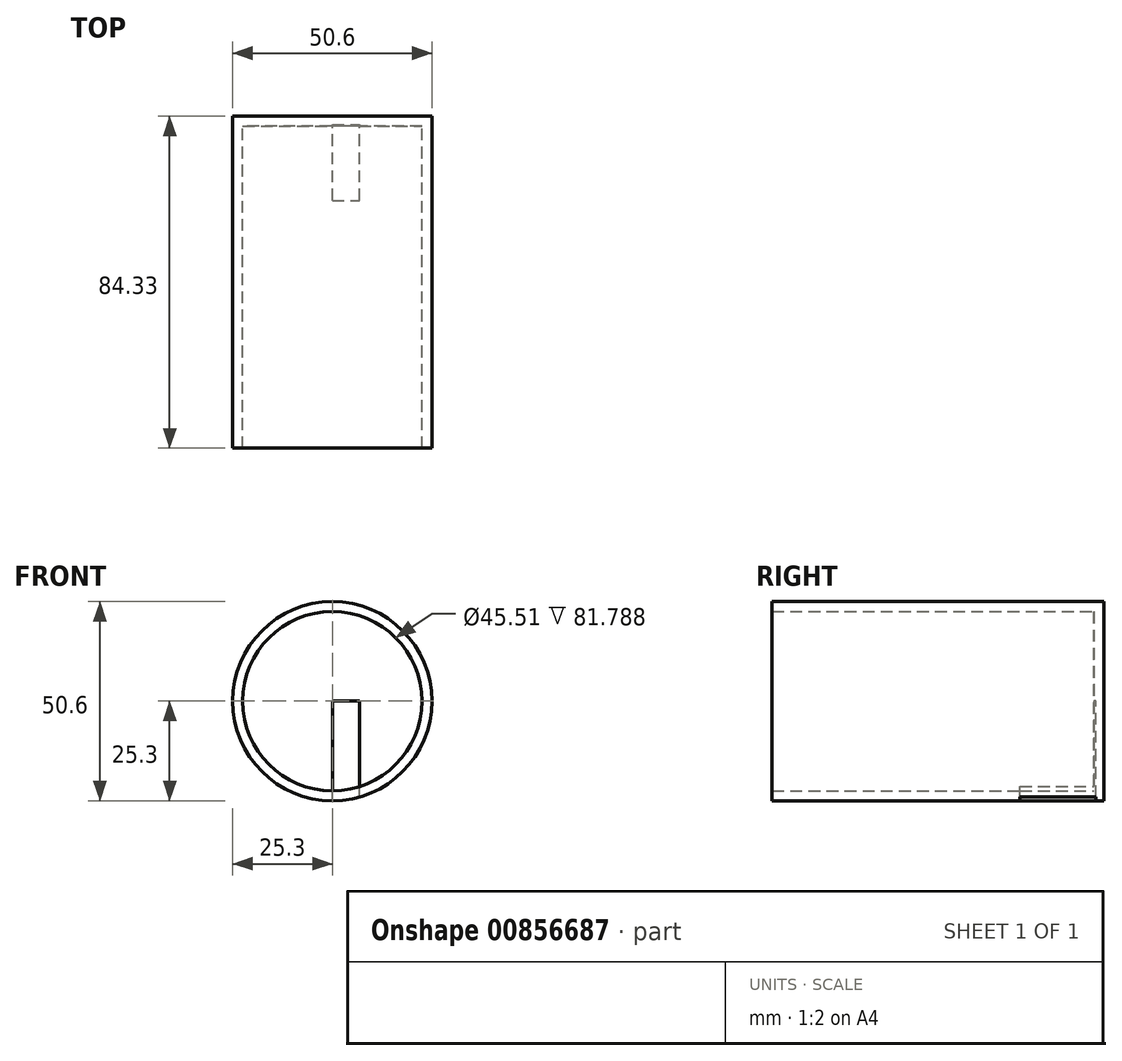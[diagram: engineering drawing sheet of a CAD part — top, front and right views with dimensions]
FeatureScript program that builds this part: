
annotation { "Feature Type Name" : "Feature", "Feature Type Description" : "" }
export const myFeature = defineFeature(function(context is Context, id is Id, definition is map)
    precondition{}
    {
        {
            var Q0;
            Q0=qCreatedBy(makeId("Front.planeOp"),FACE);
            var sketch = newSketch(context, id + "F0", { "sketchPlane" : qUnion([Q0])});
            skCircle(sketch, "E0", {"center": v(0, 0) * mm, "radius": 25.3 * mm});
            skSolve(sketch);
        }
        {
            var Q0;
            Q0 = qSketchRegion(id + "F0", true);
            extrude(context, id + "F1", {"entities" : qUnion([Q0]), "depth" : 84.33 * mm, "offsetDistance" : 25.4 * mm});
        }
        {
            var Q0;
            Q0=makeQuery(id+"F1.opExtrude","CAP_FACE",FACE,{"disambiguationData":[OSD([sQuery(id+"F0.wireOp",EDGE,"E0")])],"isStart":false});
            shell(context, id + "F2", {"entities" : qUnion([Q0]), "thickness" : 2.54 * mm});
        }
        {
            var Q0;
            Q0=qCreatedBy(makeId("Top.planeOp"),FACE);
            var sketch = newSketch(context, id + "F3", { "sketchPlane" : qUnion([Q0])});
            skLineSegment(sketch, "E1.bottom", {"start": v(0, -2.11) * mm, "end": v(6.89, -2.11) * mm});
            skLineSegment(sketch, "E1.top", {"start": v(0, -21.4) * mm, "end": v(6.89, -21.4) * mm});
            skLineSegment(sketch, "E1.left", {"start": v(0, -2.11) * mm, "end": v(0, -21.4) * mm});
            skLineSegment(sketch, "E1.right", {"start": v(6.89, -2.11) * mm, "end": v(6.89, -21.4) * mm});
            skSolve(sketch);
        }
        {
            var Q0;
            Q0 = qSketchRegion(id + "F3", true);
            extrude(context, id + "F4", {"entities" : qUnion([Q0]), "operationType" : NewBodyOperationType.REMOVE, "oppositeDirection" : true, "depth" : 25.4 * mm, "offsetDistance" : 25.4 * mm});
        }
    });
